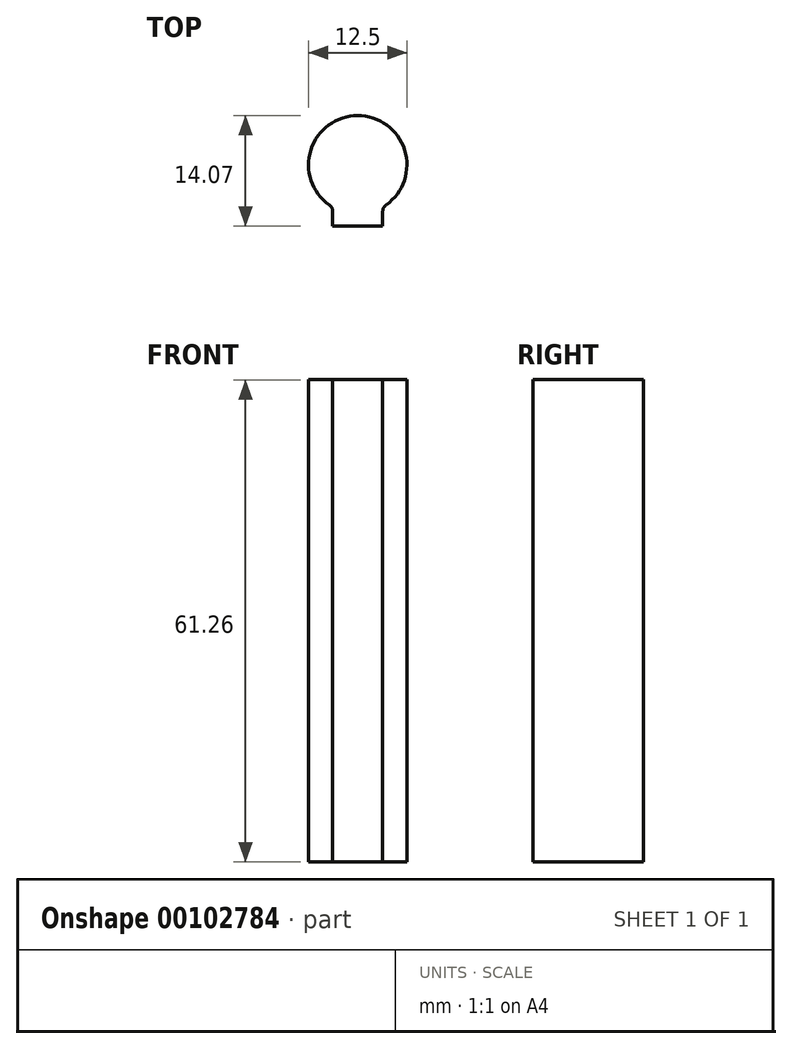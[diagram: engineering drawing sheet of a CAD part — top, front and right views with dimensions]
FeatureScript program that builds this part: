
annotation { "Feature Type Name" : "Feature", "Feature Type Description" : "" }
export const myFeature = defineFeature(function(context is Context, id is Id, definition is map)
    precondition{}
    {
        {
            var Q0;
            Q0=qCreatedBy(makeId("Top.planeOp"),FACE);
            var sketch = newSketch(context, id + "F0", { "sketchPlane" : qUnion([Q0])});
            skLineSegment(sketch, "E0.bottom", {"start": v(3.18, -7.82) * mm, "end": v(-3.17, -7.82) * mm});
            skPoint(sketch, "E0.middle", {"position": v(0, 0) * mm});
            skArc(sketch, "E1", {"start": v(3.18, -5.38) * mm, "mid": v(0, 6.25) * mm, "end": v(-3.17, -5.38) * mm});
            skLineSegment(sketch, "E2", {"start": v(-3.17, -5.38) * mm, "end": v(-3.17, -7.82) * mm});
            skLineSegment(sketch, "E3", {"start": v(-3.17, -7.82) * mm, "end": v(3.18, -7.82) * mm});
            skLineSegment(sketch, "E4", {"start": v(3.18, -7.82) * mm, "end": v(3.18, -5.38) * mm});
            skPoint(sketch, "E0.left.end.orphan", {"position": v(8.1, 7.82) * mm});
            skPoint(sketch, "E5.orphan", {"position": v(6.94, -7.82) * mm});
            skPoint(sketch, "E0.right.end.orphan", {"position": v(-6.94, 7.82) * mm});
            skPoint(sketch, "E6.orphan", {"position": v(-8.1, -7.82) * mm});
            skSolve(sketch);
        }
        {
            var Q0;
            {var subQ0=sQuery(id+"F0.wireOp",EDGE,"E2");Q0=makeQuery(id+"F0.imprint","IMPRINT",FACE,{"disambiguationData":[TD([[makeQuery(id+"F0.imprint","IMPRINT",EDGE,{"derivedFrom":subQ0}),1.0]])]});}
            var Q1;
            {var subQ0=sQuery(id+"F0.wireOp",EDGE,"E1");var subQ1=makeQuery(id+"F0.imprint","INTERSECT",VERTEX,{"derivedFrom":[subQ0,sQuery(id+"F0.wireOp",EDGE,"E2")]});Q1=makeQuery(id+"F0.imprint","IMPRINT",FACE,{"disambiguationData":[TD([[makeQuery(id+"F0.imprint","IMPRINT",EDGE,{"disambiguationData":[TD([[subQ1,-1.0]])],"derivedFrom":subQ0}),1.0]])]});}
            extrude(context, id + "F1", {"entities" : qUnion([Q0, Q1]), "depth" : 61.26 * mm});
        }
        {
            var Q0;
            Q0=makeQuery(id+"F1.opExtrude","SWEPT_EDGE",EDGE,{"disambiguationData":[OSD([sQuery(id+"F0.wireOp",EDGE,"E1"),sQuery(id+"F0.wireOp",EDGE,"E2")])]});
            var Q1;
            Q1=makeQuery(id+"F1.opExtrude","SWEPT_EDGE",EDGE,{"disambiguationData":[OSD([sQuery(id+"F0.wireOp",EDGE,"E1"),sQuery(id+"F0.wireOp",EDGE,"E4")])]});
            fillet(context, id + "F2", {"entities" : qUnion([Q0, Q1]), "radius" : 1.02 * mm, "tangentPropagation" : true, "allowEdgeOverflow" : false});
        }
    });
